# Revit family: WAGNER_Клипса
name_source: partatom
category: Арматура трубопроводов
revit_build: Autodesk Revit 2017 (Build: 20190508_0315(x64)
units: mm (PartAtom-declared; Revit-internal decimal feet)

## family parameters
Всегда вертикально = Да
Заголовок OmniClass = Pipework/Ductwork Mechanical Fasteners/Supports
На основе рабочей плоскости = Нет
Номер OmniClass = 23.60.30.11.17
Общий = Да
При загрузке вырезать с полостями = Нет
Размер круглого соединителя = Использовать диаметр
Тип детали = Вставляется

## types (1)
- Typ NG 23 VE=100 Stk
    ADSK_URL документации изделия = https://ru.wagnergroup.com
    ADSK_URL страницы изделия = https://ru.wagnergroup.com
    ADSK_Версия Revit = Revit 2017
    ADSK_Версия семейства = Версия 1
    ADSK_Дата изменения = 18.07.20
    ADSK_Единица измерения = шт.
    ADSK_Завод-изготовитель = WAGNER
    ADSK_Код изделия = -
    ADSK_Марка = Typ NG 23 VE=100 Stk
    ADSK_Материал = WAGNER_PVC
    ADSK_Наименование = Крепёжная клипса
    ADSK_Наименование краткое = Клипса
    ADSK_Размер_Высота = 0 мм
    ADSK_Размер_Длина = 0 мм
    ADSK_Размер_Ширина = 0 мм
    COBie Category = Pipework Fittings
    Masterformat Code = 22 05 29
    Masterformat Title = Hangers and supports for pipe and equipment
    OmniClass Code = 23-13 23 11 13
    OmniClass Title = Multi Purpose Mechanical Fasteners
    UNSPSC Code = 31160000
    UNSPSC Title = Tube Clip
    URL = www.wagner-russia.com
    Uniclass Code = Pr_65_52_61_62
    Uniclass Title = Pipeline supports
    WAGNER_Variation = 1
    WAGNER_Артикул = 01-35-1075
    WAGNER_Название = Крепёжная клипса
    WAGNER_Температурный режим. = от -20℃ до +60℃
    WAGNER_Тип = Typ NG 23 VE=100 Stk
    bimon.ru = bimon.ru
    Изготовитель = WAGNER
    Описание = Крепёжная клипса
